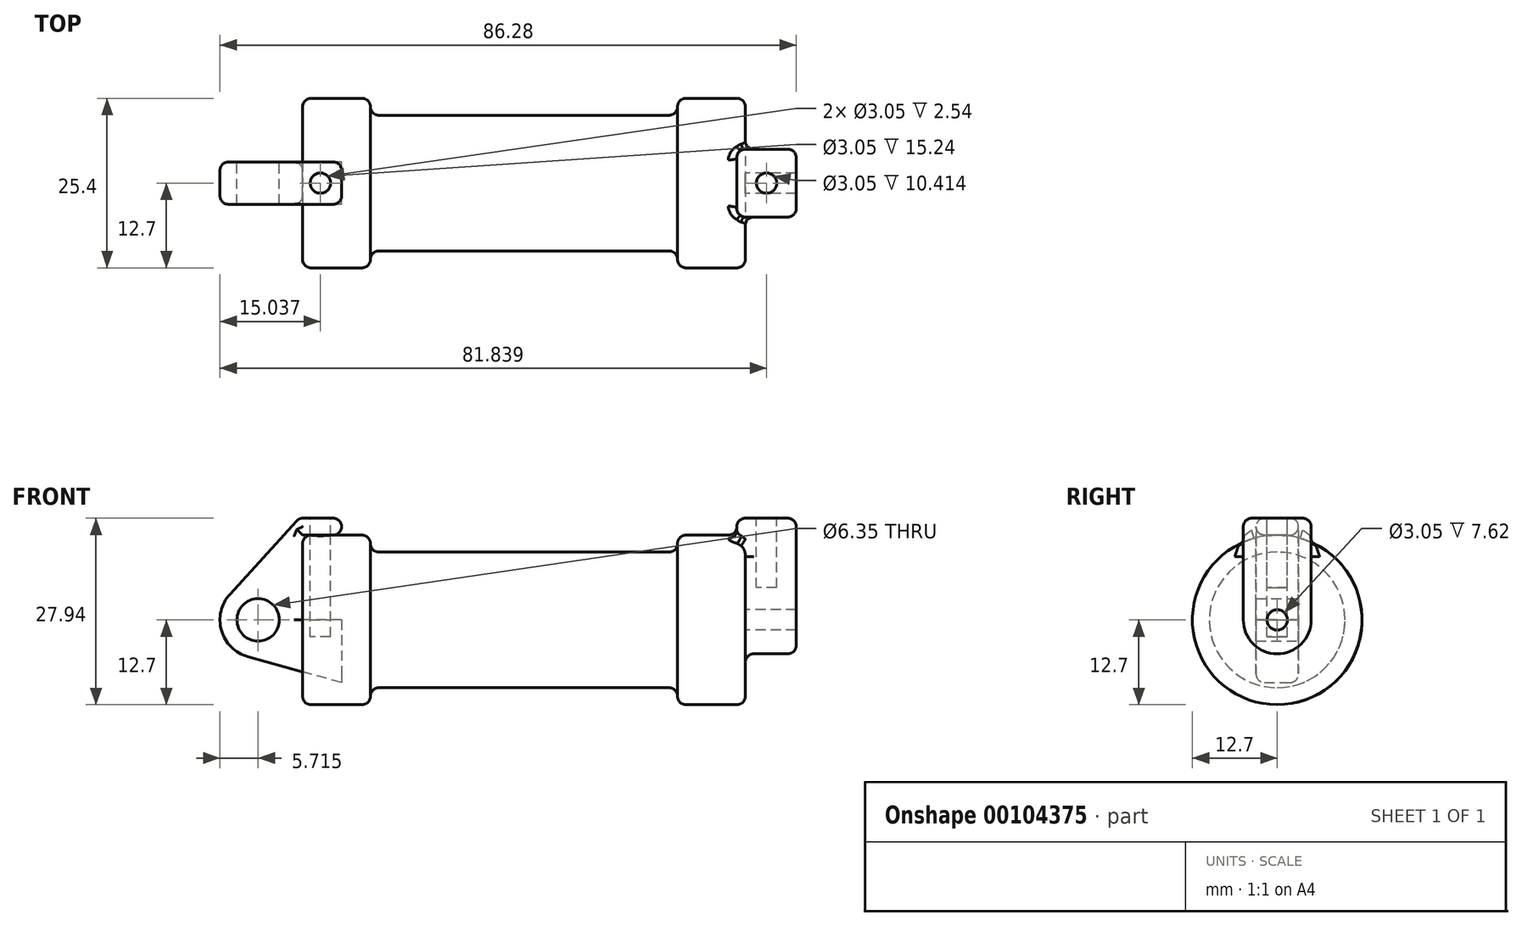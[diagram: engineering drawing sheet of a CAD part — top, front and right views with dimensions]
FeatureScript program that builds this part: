
annotation { "Feature Type Name" : "Feature", "Feature Type Description" : "" }
export const myFeature = defineFeature(function(context is Context, id is Id, definition is map)
    precondition{}
    {
        {
            var Q0;
            Q0=qCreatedBy(makeId("Front.planeOp"),FACE);
            var sketch = newSketch(context, id + "F0", { "sketchPlane" : qUnion([Q0])});
            skLineSegment(sketch, "E0", {"start": v(0, 0) * mm, "end": v(0, 12.7) * mm});
            skLineSegment(sketch, "E1", {"start": v(0, 12.7) * mm, "end": v(10.16, 12.7) * mm});
            skLineSegment(sketch, "E2", {"start": v(10.16, 12.7) * mm, "end": v(10.16, 10.16) * mm});
            skLineSegment(sketch, "E3", {"start": v(10.16, 10.16) * mm, "end": v(56.13, 10.16) * mm});
            skLineSegment(sketch, "E4", {"start": v(56.13, 10.16) * mm, "end": v(56.13, 12.7) * mm});
            skLineSegment(sketch, "E5", {"start": v(56.13, 12.7) * mm, "end": v(66.3, 12.7) * mm});
            skLineSegment(sketch, "E6", {"start": v(66.3, 12.7) * mm, "end": v(66.3, 0) * mm});
            skLineSegment(sketch, "E7", {"start": v(66.3, 0) * mm, "end": v(0, 0) * mm});
            skLineSegment(sketch, "E8", {"start": v(5.84, 15.24) * mm, "end": v(-0.5, 15.24) * mm});
            skLineSegment(sketch, "E9", {"start": v(-0.5, 15.24) * mm, "end": v(-10.88, 3.85) * mm});
            skLineSegment(sketch, "E10", {"start": v(0, 0) * mm, "end": v(-6.65, 0) * mm});
            skCircle(sketch, "E11", {"center": v(-6.65, 0) * mm, "radius": 5.72 * mm});
            skCircle(sketch, "E12", {"center": v(-6.65, 0) * mm, "radius": 3.18 * mm});
            skLineSegment(sketch, "E13", {"start": v(5.84, 15.24) * mm, "end": v(5.84, -9.4) * mm});
            skLineSegment(sketch, "E14", {"start": v(5.84, -9.4) * mm, "end": v(-8.18, -5.5) * mm});
            skSolve(sketch);
        }
        {
            var Q0;
            {var subQ0=sQuery(id+"F0.wireOp",EDGE,"E2");Q0=makeQuery(id+"F0.imprint","IMPRINT",FACE,{"disambiguationData":[TD([[makeQuery(id+"F0.imprint","IMPRINT",EDGE,{"derivedFrom":subQ0}),-1.0]])]});}
            var Q1;
            {var subQ0=sQuery(id+"F0.wireOp",EDGE,"E0");Q1=makeQuery(id+"F0.imprint","IMPRINT",FACE,{"disambiguationData":[TD([[makeQuery(id+"F0.imprint","IMPRINT",EDGE,{"derivedFrom":subQ0}),-1.0]])]});}
            var Q2;
            Q2=sQuery(id+"F0.wireOp",EDGE,"E7");
            revolve(context, id + "F1", {"entities" : qUnion([Q0, Q1]), "axis" : qUnion([Q2]), "revolveType" : RevolveType.FULL});
        }
        {
            var Q0;
            {var subQ4=sQuery(id+"F0.wireOp",EDGE,"E12");Q0=makeQuery(id+"F0.imprint","IMPRINT",FACE,{"disambiguationData":[TD([[makeQuery(id+"F0.imprint","IMPRINT",EDGE,{"derivedFrom":subQ4}),-1.0]])]});}
            var Q1;
            {var subQ3=sQuery(id+"F0.wireOp",EDGE,"E0");Q1=makeQuery(id+"F0.imprint","IMPRINT",FACE,{"disambiguationData":[TD([[makeQuery(id+"F0.imprint","IMPRINT",EDGE,{"derivedFrom":subQ3}),1.0]])]});}
            var Q2;
            {var subQ0=sQuery(id+"F0.wireOp",EDGE,"E14");Q2=makeQuery(id+"F0.imprint","IMPRINT",FACE,{"disambiguationData":[TD([[makeQuery(id+"F0.imprint","IMPRINT",EDGE,{"derivedFrom":subQ0}),-1.0]])]});}
            extrude(context, id + "F2", {"entities" : qUnion([Q0, Q1, Q2]), "endBound" : BoundingType.SYMMETRIC, "depth" : 6.35 * mm});
        }
        {
            var Q0;
            Q0=makeQuery(id+"F1.opRevolve","SWEPT_FACE",FACE,{"disambiguationData":[OSD([sQuery(id+"F0.wireOp",EDGE,"E6")])]});
            var sketch = newSketch(context, id + "F3", { "sketchPlane" : qUnion([Q0])});
            skCircle(sketch, "E15", {"center": v(0, 0) * mm, "radius": 1.52 * mm});
            skCircle(sketch, "E16", {"center": v(0, 0) * mm, "radius": 5.08 * mm});
            skLineSegment(sketch, "E17", {"start": v(-5.08, 0) * mm, "end": v(-5.08, 15.24) * mm});
            skLineSegment(sketch, "E18", {"start": v(5.08, 0) * mm, "end": v(5.08, 15.24) * mm});
            skLineSegment(sketch, "E19", {"start": v(5.08, 15.24) * mm, "end": v(-5.08, 15.24) * mm});
            skSolve(sketch);
        }
        {
            var Q0;
            Q0 = qSketchRegion(id + "F3", true);
            extrude(context, id + "F4", {"entities" : qUnion([Q0]), "operationType" : NewBodyOperationType.ADD, "depth" : 7.62 * mm, "hasSecondDirection" : true, "secondDirectionOppositeDirection" : true, "secondDirectionDepth" : 1.27 * mm});
        }
        {
            var Q0;
            Q0=makeQuery(id+"F4.opExtrude","SWEPT_FACE",FACE,{"disambiguationData":[OSD([sQuery(id+"F3.wireOp",EDGE,"E19")])]});
            var sketch = newSketch(context, id + "F5", { "sketchPlane" : qUnion([Q0])});
            skCircle(sketch, "E20", {"center": v(69.47, 0) * mm, "radius": 1.52 * mm});
            skSolve(sketch);
        }
        {
            var Q0;
            Q0=makeQuery(id+"F2.opExtrude","SWEPT_FACE",FACE,{"disambiguationData":[OSD([sQuery(id+"F0.wireOp",EDGE,"E8")])]});
            var sketch = newSketch(context, id + "F6", { "sketchPlane" : qUnion([Q0])});
            skCircle(sketch, "E21", {"center": v(2.67, 0) * mm, "radius": 1.52 * mm});
            skSolve(sketch);
        }
        {
            var Q0;
            Q0=makeQuery(id+"F6.imprint","IMPRINT",FACE,{"disambiguationData":[TD([[makeQuery(id+"F6.imprint","IMPRINT",EDGE,{"derivedFrom":sQuery(id+"F6.wireOp",EDGE,"E21")}),1.0]])]});
            extrude(context, id + "F7", {"entities" : qUnion([Q0]), "operationType" : NewBodyOperationType.REMOVE, "oppositeDirection" : true, "depth" : 17.78 * mm});
        }
        {
            var Q0;
            Q0=makeQuery(id+"F5.imprint","IMPRINT",FACE,{"disambiguationData":[TD([[makeQuery(id+"F5.imprint","IMPRINT",EDGE,{"derivedFrom":sQuery(id+"F5.wireOp",EDGE,"E20")}),1.0]])]});
            extrude(context, id + "F8", {"entities" : qUnion([Q0]), "operationType" : NewBodyOperationType.REMOVE, "oppositeDirection" : true, "depth" : 10.4 * mm});
        }
        {
            var Q0;
            Q0=makeQuery(id+"F2.opExtrude","CAP_EDGE",EDGE,{"disambiguationData":[OSD([sQuery(id+"F0.wireOp",EDGE,"E9")])],"isStart":true});
            var Q1;
            {var subQ0=sQuery(id+"F0.wireOp",EDGE,"E13");Q1=makeQuery(id+"F2.opExtrude","CAP_EDGE",EDGE,{"disambiguationData":[OSD([subQ0]),TDD([makeQuery(id+"F0.imprint","IMPRINT",EDGE,{"disambiguationData":[TD([[makeQuery(id+"F0.imprint","INTERSECT",VERTEX,{"derivedFrom":[sQuery(id+"F0.wireOp",EDGE,"E8"),subQ0]}),-1.0]])],"derivedFrom":subQ0})])],"isStart":true});}
            var Q2;
            Q2=makeQuery(id+"F2.opExtrude","SWEPT_EDGE",EDGE,{"disambiguationData":[OSD([sQuery(id+"F0.wireOp",EDGE,"E8"),sQuery(id+"F0.wireOp",EDGE,"E9")])]});
            var Q3;
            Q3=makeQuery(id+"F2.opExtrude","CAP_EDGE",EDGE,{"disambiguationData":[OSD([sQuery(id+"F0.wireOp",EDGE,"E8")])],"isStart":true});
            var Q4;
            Q4=makeQuery(id+"F2.opExtrude","CAP_EDGE",EDGE,{"disambiguationData":[OSD([sQuery(id+"F0.wireOp",EDGE,"E1")])],"isStart":true});
            var Q5;
            Q5=makeQuery(id+"F2.opExtrude","CAP_EDGE",EDGE,{"disambiguationData":[OSD([sQuery(id+"F0.wireOp",EDGE,"E0")])],"isStart":true});
            var Q6;
            Q6=makeQuery(id+"F1.opRevolve","SWEPT_EDGE",EDGE,{"disambiguationData":[OSD([sQuery(id+"F0.wireOp",EDGE,"E0"),sQuery(id+"F0.wireOp",EDGE,"E1")])]});
            var Q7;
            Q7=makeQuery(id+"F2.opExtrude","CAP_EDGE",EDGE,{"disambiguationData":[OSD([sQuery(id+"F0.wireOp",EDGE,"E9")])],"isStart":false});
            var Q8;
            Q8=makeQuery(id+"F2.opExtrude","CAP_EDGE",EDGE,{"disambiguationData":[OSD([sQuery(id+"F0.wireOp",EDGE,"E11")])],"isStart":true});
            var Q9;
            Q9=makeQuery(id+"F2.opExtrude","CAP_EDGE",EDGE,{"disambiguationData":[OSD([sQuery(id+"F0.wireOp",EDGE,"E11")])],"isStart":false});
            var Q10;
            Q10=makeQuery(id+"F2.opExtrude","CAP_EDGE",EDGE,{"disambiguationData":[OSD([sQuery(id+"F0.wireOp",EDGE,"E14")])],"isStart":true});
            var Q11;
            Q11=makeQuery(id+"F2.opExtrude","CAP_EDGE",EDGE,{"disambiguationData":[OSD([sQuery(id+"F0.wireOp",EDGE,"E0")])],"isStart":false});
            var Q12;
            Q12=makeQuery(id+"F2.opExtrude","CAP_EDGE",EDGE,{"disambiguationData":[OSD([sQuery(id+"F0.wireOp",EDGE,"E1")])],"isStart":false});
            var Q13;
            Q13=makeQuery(id+"F2.opExtrude","CAP_EDGE",EDGE,{"disambiguationData":[OSD([sQuery(id+"F0.wireOp",EDGE,"E8")])],"isStart":false});
            var Q14;
            {var subQ0=sQuery(id+"F0.wireOp",EDGE,"E13");Q14=makeQuery(id+"F2.opExtrude","CAP_EDGE",EDGE,{"disambiguationData":[OSD([subQ0]),TDD([makeQuery(id+"F0.imprint","IMPRINT",EDGE,{"disambiguationData":[TD([[makeQuery(id+"F0.imprint","INTERSECT",VERTEX,{"derivedFrom":[sQuery(id+"F0.wireOp",EDGE,"E8"),subQ0]}),-1.0]])],"derivedFrom":subQ0})])],"isStart":false});}
            var Q15;
            Q15=makeQuery(id+"F2.opExtrude","SWEPT_EDGE",EDGE,{"disambiguationData":[OSD([sQuery(id+"F0.wireOp",EDGE,"E8"),sQuery(id+"F0.wireOp",EDGE,"E13")])]});
            var Q16;
            Q16=makeQuery(id+"F2.opExtrude","SWEPT_EDGE",EDGE,{"disambiguationData":[OSD([sQuery(id+"F0.wireOp",EDGE,"E1"),sQuery(id+"F0.wireOp",EDGE,"E13")])]});
            fillet(context, id + "F9", {"entities" : qUnion([Q0, Q1, Q2, Q3, Q4, Q5, Q6, Q7, Q8, Q9, Q10, Q11, Q12, Q13, Q14, Q15, Q16]), "radius" : 1.27 * mm, "tangentPropagation" : true, "allowEdgeOverflow" : false});
        }
        {
            var Q0;
            Q0=makeQuery(id+"F1.opRevolve","SWEPT_EDGE",EDGE,{"disambiguationData":[OSD([sQuery(id+"F0.wireOp",EDGE,"E2"),sQuery(id+"F0.wireOp",EDGE,"E3")])]});
            var Q1;
            Q1=makeQuery(id+"F1.opRevolve","SWEPT_EDGE",EDGE,{"disambiguationData":[OSD([sQuery(id+"F0.wireOp",EDGE,"E1"),sQuery(id+"F0.wireOp",EDGE,"E2")])]});
            var Q2;
            Q2=makeQuery(id+"F1.opRevolve","SWEPT_EDGE",EDGE,{"disambiguationData":[OSD([sQuery(id+"F0.wireOp",EDGE,"E4"),sQuery(id+"F0.wireOp",EDGE,"E5")])]});
            var Q3;
            Q3=makeQuery(id+"F1.opRevolve","SWEPT_EDGE",EDGE,{"disambiguationData":[OSD([sQuery(id+"F0.wireOp",EDGE,"E3"),sQuery(id+"F0.wireOp",EDGE,"E4")])]});
            var Q4;
            Q4=makeQuery(id+"F1.opRevolve","SWEPT_EDGE",EDGE,{"disambiguationData":[OSD([sQuery(id+"F0.wireOp",EDGE,"E5"),sQuery(id+"F0.wireOp",EDGE,"E6")])]});
            fillet(context, id + "F10", {"entities" : qUnion([Q0, Q1, Q2, Q3, Q4]), "radius" : 1.27 * mm, "tangentPropagation" : true, "allowEdgeOverflow" : false});
        }
        {
            var Q0;
            Q0=makeQuery(id+"F4.opExtrude","CAP_EDGE",EDGE,{"disambiguationData":[OSD([sQuery(id+"F3.wireOp",EDGE,"E18")])],"isStart":false});
            var Q1;
            Q1=makeQuery(id+"F4.opExtrude","CAP_EDGE",EDGE,{"disambiguationData":[OSD([sQuery(id+"F3.wireOp",EDGE,"E19")])],"isStart":false});
            var Q2;
            Q2=makeQuery(id+"F4.opExtrude","CAP_EDGE",EDGE,{"disambiguationData":[OSD([sQuery(id+"F3.wireOp",EDGE,"E19")])],"isStart":true});
            var Q3;
            Q3=makeQuery(id+"F4.opExtrude","CAP_EDGE",EDGE,{"disambiguationData":[OSD([sQuery(id+"F3.wireOp",EDGE,"E17")])],"isStart":true});
            var Q4;
            Q4=makeQuery(id+"F4.opExtrude","SWEPT_EDGE",EDGE,{"disambiguationData":[OSD([sQuery(id+"F3.wireOp",EDGE,"E17"),sQuery(id+"F3.wireOp",EDGE,"E19")])]});
            var Q5;
            Q5=makeQuery(id+"F4.boolean.opBoolean","INTERSECT",EDGE,{"derivedFrom":[makeQuery(id+"F1.opRevolve","SWEPT_FACE",FACE,{"disambiguationData":[OSD([sQuery(id+"F0.wireOp",EDGE,"E6")])]}),makeQuery(id+"F4.opExtrude","SWEPT_FACE",FACE,{"disambiguationData":[OSD([sQuery(id+"F3.wireOp",EDGE,"E17")])]})]});
            var Q6;
            Q6=makeQuery(id+"F10.opFillet","BLEND_EDGE",EDGE,{"blendedFrom":[makeQuery(id+"F1.opRevolve","SWEPT_EDGE",EDGE,{"disambiguationData":[OSD([sQuery(id+"F0.wireOp",EDGE,"E5"),sQuery(id+"F0.wireOp",EDGE,"E6")])]}),makeQuery(id+"F4.opExtrude","SWEPT_FACE",FACE,{"disambiguationData":[OSD([sQuery(id+"F3.wireOp",EDGE,"E17")])]})],"blendedInto":[makeQuery(id+"F4.opExtrude","SWEPT_FACE",FACE,{"disambiguationData":[OSD([sQuery(id+"F3.wireOp",EDGE,"E17")])]})]});
            var Q7;
            Q7=makeQuery(id+"F4.opExtrude","CAP_EDGE",EDGE,{"disambiguationData":[OSD([sQuery(id+"F3.wireOp",EDGE,"E17")])],"isStart":false});
            var Q8;
            Q8=makeQuery(id+"F4.opExtrude","CAP_EDGE",EDGE,{"disambiguationData":[OSD([sQuery(id+"F3.wireOp",EDGE,"E16")])],"isStart":false});
            var Q9;
            Q9=makeQuery(id+"F4.boolean.opBoolean","INTERSECT",EDGE,{"derivedFrom":[makeQuery(id+"F1.opRevolve","SWEPT_FACE",FACE,{"disambiguationData":[OSD([sQuery(id+"F0.wireOp",EDGE,"E6")])]}),makeQuery(id+"F4.opExtrude","SWEPT_FACE",FACE,{"disambiguationData":[OSD([sQuery(id+"F3.wireOp",EDGE,"E16")])]})]});
            var Q10;
            Q10=makeQuery(id+"F4.opExtrude","CAP_EDGE",EDGE,{"disambiguationData":[OSD([sQuery(id+"F3.wireOp",EDGE,"E18")])],"isStart":true});
            var Q11;
            Q11=makeQuery(id+"F4.opExtrude","SWEPT_EDGE",EDGE,{"disambiguationData":[OSD([sQuery(id+"F3.wireOp",EDGE,"E18"),sQuery(id+"F3.wireOp",EDGE,"E19")])]});
            var Q12;
            Q12=makeQuery(id+"F4.boolean.opBoolean","INTERSECT",EDGE,{"derivedFrom":[makeQuery(id+"F1.opRevolve","SWEPT_FACE",FACE,{"disambiguationData":[OSD([sQuery(id+"F0.wireOp",EDGE,"E6")])]}),makeQuery(id+"F4.opExtrude","SWEPT_FACE",FACE,{"disambiguationData":[OSD([sQuery(id+"F3.wireOp",EDGE,"E18")])]})]});
            var Q13;
            Q13=makeQuery(id+"F10.opFillet","BLEND_EDGE",EDGE,{"blendedFrom":[makeQuery(id+"F1.opRevolve","SWEPT_EDGE",EDGE,{"disambiguationData":[OSD([sQuery(id+"F0.wireOp",EDGE,"E5"),sQuery(id+"F0.wireOp",EDGE,"E6")])]}),makeQuery(id+"F4.opExtrude","SWEPT_FACE",FACE,{"disambiguationData":[OSD([sQuery(id+"F3.wireOp",EDGE,"E18")])]})],"blendedInto":[makeQuery(id+"F4.opExtrude","SWEPT_FACE",FACE,{"disambiguationData":[OSD([sQuery(id+"F3.wireOp",EDGE,"E18")])]})]});
            var Q14;
            Q14=makeQuery(id+"F4.boolean.opBoolean","INTERSECT",EDGE,{"derivedFrom":[makeQuery(id+"F1.opRevolve","SWEPT_FACE",FACE,{"disambiguationData":[OSD([sQuery(id+"F0.wireOp",EDGE,"E5")])]}),makeQuery(id+"F4.opExtrude","CAP_FACE",FACE,{"disambiguationData":[OSD([sQuery(id+"F3.wireOp",EDGE,"E15"),sQuery(id+"F3.wireOp",EDGE,"E16"),sQuery(id+"F3.wireOp",EDGE,"E17"),sQuery(id+"F3.wireOp",EDGE,"E18"),sQuery(id+"F3.wireOp",EDGE,"E19")])],"isStart":true})]});
            fillet(context, id + "F11", {"entities" : qUnion([Q0, Q1, Q2, Q3, Q4, Q5, Q6, Q7, Q8, Q9, Q10, Q11, Q12, Q13, Q14]), "radius" : 1.27 * mm, "tangentPropagation" : true, "allowEdgeOverflow" : false});
        }
    });
